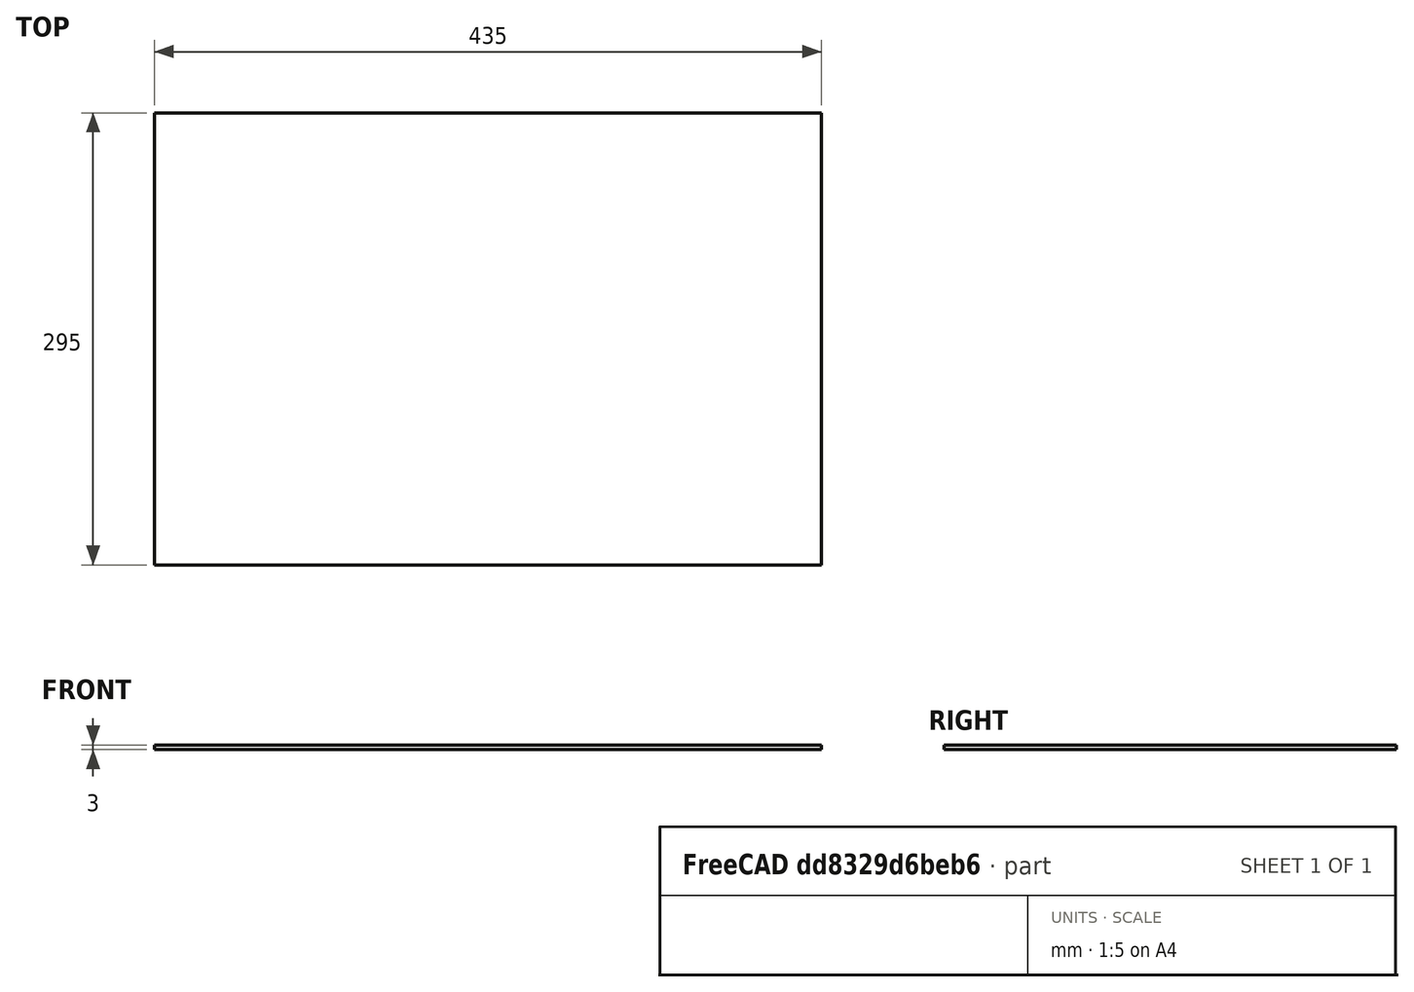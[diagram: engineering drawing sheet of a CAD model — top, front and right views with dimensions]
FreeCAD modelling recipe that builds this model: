
FCSTD DOCUMENT  (FreeCAD 0.20R29603 (Git))
Label: Scheibe-Fenster_Doppelglas_440x300
License: All rights reserved
LicenseURL: http://en.wikipedia.org/wiki/All_rights_reserved
objects: Sketcher::SketchObject×1, PartDesign::Pad×1, PartDesign::Body×1
note: 4 computed .brp shape members not serialized (recipe doc carries the construction recipe); baked Part::Feature solids carry a one-line shape summary decoded from their .brp

FEATURE [Sketcher::SketchObject] Sketch
  FullyConstrained = true
  MapMode = 5
  Support = -> [XY_Plane]
  sketch-geometry (5):
    g0: LineSegment StartX=-217.5 StartY=147.5 StartZ=0 EndX=-217.5 EndY=-147.5 EndZ=0
    g1: LineSegment StartX=-217.5 StartY=-147.5 StartZ=0 EndX=217.5 EndY=-147.5 EndZ=0
    g2: LineSegment StartX=217.5 StartY=-147.5 StartZ=0 EndX=217.5 EndY=147.5 EndZ=0
    g3: LineSegment StartX=217.5 StartY=147.5 StartZ=0 EndX=-217.5 EndY=147.5 EndZ=0
    g4: GeomPoint X=0 Y=0 Z=0
  constraints (12):
    c: Coincident(g0,g1)
    c: Coincident(g1,g2)
    c: Coincident(g2,g3)
    c: Coincident(g3,g0)
    c: Horizontal(g1)
    c: Horizontal(g3)
    c: Vertical(g0)
    c: Vertical(g2)
    c: Symmetric(g1,g0,g4)
    c: Coincident(g4,g-1)
    c: Distance(g3) = 435
    c: Distance(g2) = 295
FEATURE [PartDesign::Pad] Pad
  Direction = (0,0,1)
  Length = 3
  Length2 = 10
  Profile = -> Sketch
  ReferenceAxis = -> Sketch [N_Axis]
  Type = 0
FEATURE [PartDesign::Body] Body
  Group = -> [Sketch,Pad]
  Origin = -> Origin
  Tip = -> Pad
